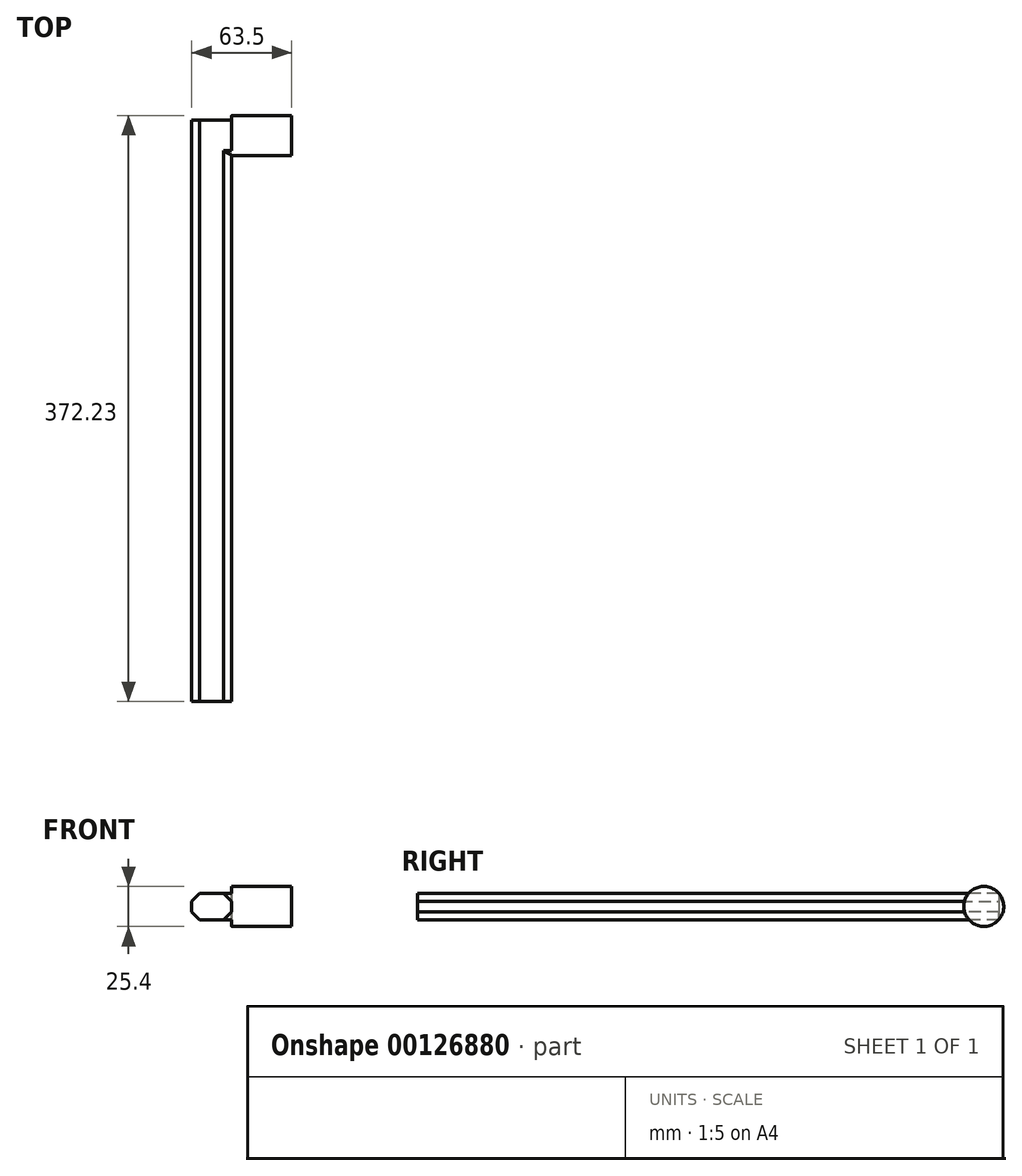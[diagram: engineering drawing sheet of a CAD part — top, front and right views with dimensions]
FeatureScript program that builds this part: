
annotation { "Feature Type Name" : "Feature", "Feature Type Description" : "" }
export const myFeature = defineFeature(function(context is Context, id is Id, definition is map)
    precondition{}
    {
        {
            var Q0;
            Q0=qCreatedBy(makeId("Right.planeOp"),FACE);
            var sketch = newSketch(context, id + "F0", { "sketchPlane" : qUnion([Q0])});
            skCircle(sketch, "E0", {"center": v(5.41, 28.58) * mm, "radius": 12.7 * mm});
            skSolve(sketch);
        }
        {
            var Q0;
            Q0=makeQuery(id+"F0.imprint","IMPRINT",FACE,{"disambiguationData":[TD([[makeQuery(id+"F0.imprint","IMPRINT",EDGE,{"derivedFrom":sQuery(id+"F0.wireOp",EDGE,"E0")}),1.0]])]});
            extrude(context, id + "F1", {"entities" : qUnion([Q0]), "depth" : 38.1 * mm});
        }
        {
            var Q0;
            Q0=makeQuery(id+"F1.opExtrude","CAP_FACE",FACE,{"disambiguationData":[OSD([sQuery(id+"F0.wireOp",EDGE,"E0")])],"isStart":true});
            var sketch = newSketch(context, id + "F2", { "sketchPlane" : qUnion([Q0])});
            skLineSegment(sketch, "E1.bottom", {"start": v(-15, 36.9) * mm, "end": v(4.12, 36.9) * mm});
            skLineSegment(sketch, "E1.top", {"start": v(-15, 20.19) * mm, "end": v(4.12, 20.19) * mm});
            skLineSegment(sketch, "E1.left", {"start": v(-15, 36.9) * mm, "end": v(-15, 20.19) * mm});
            skLineSegment(sketch, "E1.right", {"start": v(4.12, 36.9) * mm, "end": v(4.12, 20.19) * mm});
            skSolve(sketch);
        }
        {
            var Q0;
            {var subQ0=sQuery(id+"F2.wireOp",EDGE,"E1.left");var subQ1=sQuery(id+"F2.wireOp",EDGE,"E1.top");var subQ2=makeQuery(id+"F2.imprint","INTERSECT",VERTEX,{"derivedFrom":[subQ1,subQ0]});Q0=makeQuery(id+"F2.imprint","IMPRINT",FACE,{"disambiguationData":[TD([[makeQuery(id+"F2.imprint","IMPRINT",EDGE,{"disambiguationData":[TD([[subQ2,-1.0]])],"derivedFrom":subQ1}),1.0]])]});}
            var Q1;
            {var subQ2=sQuery(id+"F2.wireOp",EDGE,"E1.bottom");Q1=makeQuery(id+"F2.imprint","IMPRINT",FACE,{"disambiguationData":[TD([[makeQuery(id+"F2.imprint","IMPRINT",EDGE,{"derivedFrom":subQ2}),-1.0]])]});}
            extrude(context, id + "F3", {"entities" : qUnion([Q0, Q1]), "operationType" : NewBodyOperationType.ADD, "depth" : 25.4 * mm});
        }
        {
            var Q0;
            Q0=makeQuery(id+"F3.opExtrude","SWEPT_FACE",FACE,{"disambiguationData":[OSD([sQuery(id+"F2.wireOp",EDGE,"E1.right")])]});
            var sketch = newSketch(context, id + "F4", { "sketchPlane" : qUnion([Q0])});
            skLineSegment(sketch, "E2.bottom", {"start": v(-25.4, 36.9) * mm, "end": v(0, 36.9) * mm});
            skLineSegment(sketch, "E2.top", {"start": v(-25.4, 20.19) * mm, "end": v(0, 20.19) * mm});
            skLineSegment(sketch, "E2.left", {"start": v(-25.4, 36.9) * mm, "end": v(-25.4, 20.19) * mm});
            skLineSegment(sketch, "E2.right", {"start": v(0, 36.9) * mm, "end": v(0, 20.19) * mm});
            skSolve(sketch);
        }
        {
            var Q0;
            Q0=makeQuery(id+"F4.imprint","IMPRINT",FACE,{"disambiguationData":[TD([[makeQuery(id+"F4.imprint","IMPRINT",EDGE,{"derivedFrom":sQuery(id+"F4.wireOp",EDGE,"E2.bottom")}),-1.0]])]});
            extrude(context, id + "F5", {"entities" : qUnion([Q0]), "operationType" : NewBodyOperationType.ADD, "depth" : 350 * mm});
        }
        {
            var Q0;
            Q0=makeQuery(id+"F5.boolean.opBoolean","MERGE",EDGE,{"derivedFrom":[makeQuery(id+"F3.opExtrude","CAP_EDGE",EDGE,{"disambiguationData":[OSD([sQuery(id+"F2.wireOp",EDGE,"E1.bottom")])],"isStart":false}),makeQuery(id+"F5.opExtrude","SWEPT_EDGE",EDGE,{"disambiguationData":[OSD([sQuery(id+"F4.wireOp",EDGE,"E2.bottom"),sQuery(id+"F4.wireOp",EDGE,"E2.left")])]})]});
            var Q1;
            Q1=makeQuery(id+"F5.boolean.opBoolean","MERGE",EDGE,{"derivedFrom":[makeQuery(id+"F3.opExtrude","CAP_EDGE",EDGE,{"disambiguationData":[OSD([sQuery(id+"F2.wireOp",EDGE,"E1.top")])],"isStart":false}),makeQuery(id+"F5.opExtrude","SWEPT_EDGE",EDGE,{"disambiguationData":[OSD([sQuery(id+"F4.wireOp",EDGE,"E2.top"),sQuery(id+"F4.wireOp",EDGE,"E2.left")])]})]});
            var Q2;
            Q2=makeQuery(id+"F5.opExtrude","SWEPT_EDGE",EDGE,{"disambiguationData":[OSD([sQuery(id+"F4.wireOp",EDGE,"E2.top"),sQuery(id+"F4.wireOp",EDGE,"E2.right")])]});
            var Q3;
            Q3=makeQuery(id+"F5.boolean.opBoolean","SPLIT",EDGE,{"derivedFrom":makeQuery(id+"F5.opExtrude","SWEPT_EDGE",EDGE,{"disambiguationData":[OSD([sQuery(id+"F4.wireOp",EDGE,"E2.bottom"),sQuery(id+"F4.wireOp",EDGE,"E2.right")])]})});
            chamfer(context, id + "F6", {"entities" : qUnion([Q0, Q1, Q2, Q3]), "width" : 5.08 * mm, "tangentPropagation" : true});
        }
    });
